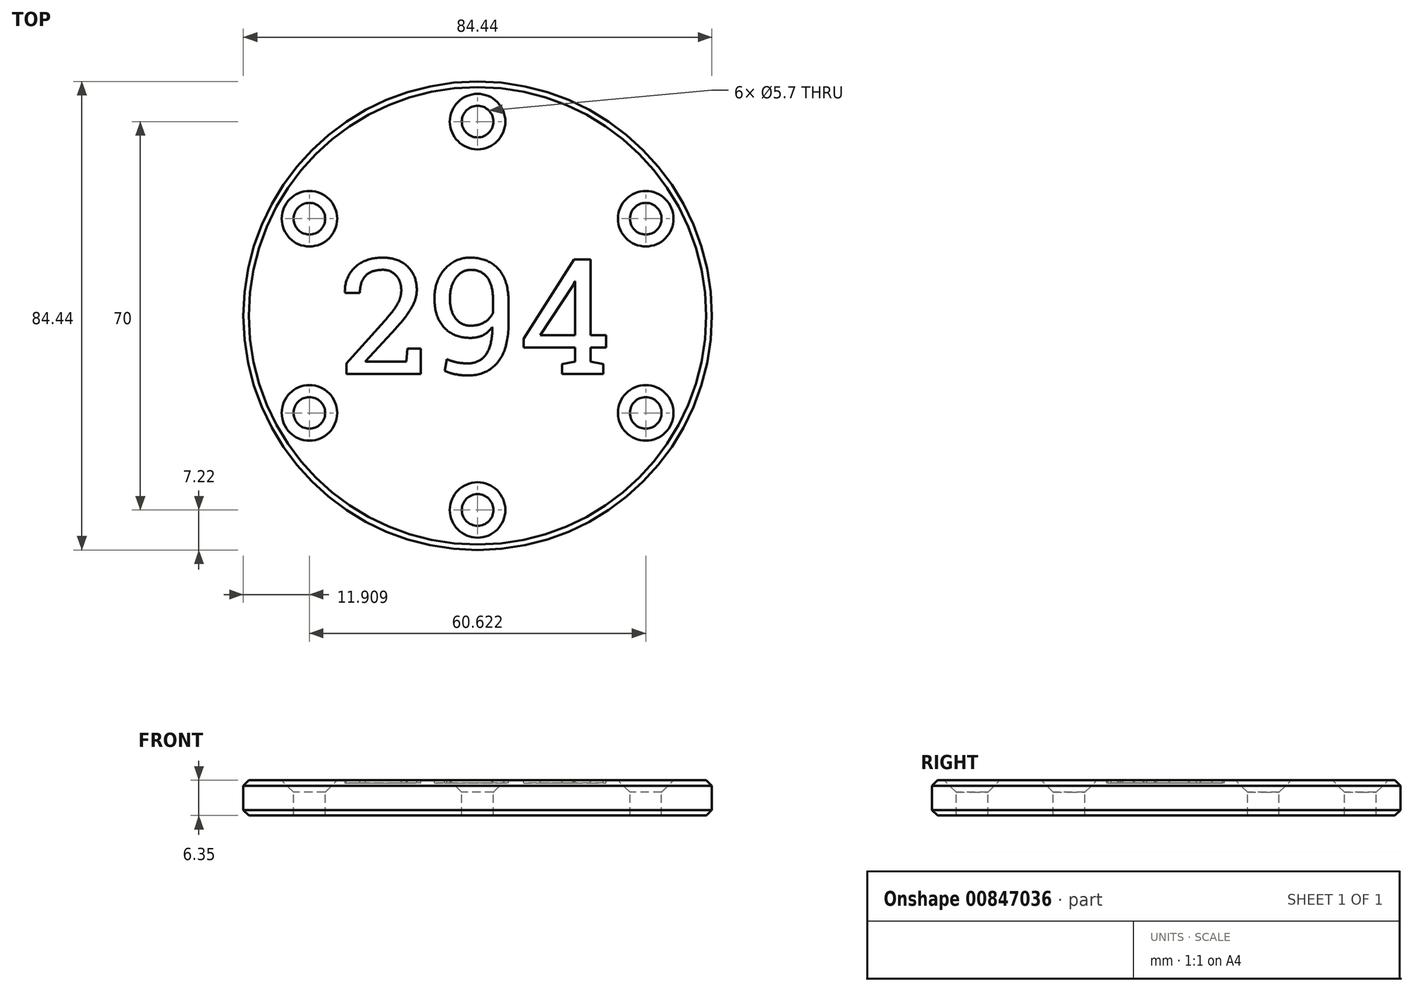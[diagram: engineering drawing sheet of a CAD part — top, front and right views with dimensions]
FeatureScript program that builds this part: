
annotation { "Feature Type Name" : "Feature", "Feature Type Description" : "" }
export const myFeature = defineFeature(function(context is Context, id is Id, definition is map)
    precondition{}
    {
        {
            var Q0;
            Q0=qCreatedBy(makeId("Top.planeOp"),FACE);
            var sketch = newSketch(context, id + "F0", { "sketchPlane" : qUnion([Q0])});
            skCircle(sketch, "E0", {"center": v(0, 0) * mm, "radius": 42.22 * mm});
            skCircle(sketch, "E1", {"center": v(0, 0) * mm, "radius": 24 * mm});
            skCircle(sketch, "E2.cCircle", {"center": v(0, 0) * mm, "radius": 35 * mm, "construction": true});
            skLineSegment(sketch, "E2.0", {"start": v(0, 35) * mm, "end": v(30.31, 17.5) * mm});
            skLineSegment(sketch, "E2.1", {"start": v(30.31, 17.5) * mm, "end": v(30.31, -17.5) * mm});
            skLineSegment(sketch, "E2.2", {"start": v(30.31, -17.5) * mm, "end": v(0, -35) * mm});
            skLineSegment(sketch, "E2.3", {"start": v(0, -35) * mm, "end": v(-30.31, -17.5) * mm});
            skLineSegment(sketch, "E2.4", {"start": v(-30.31, -17.5) * mm, "end": v(-30.31, 17.5) * mm});
            skLineSegment(sketch, "E2.5", {"start": v(-30.31, 17.5) * mm, "end": v(0, 35) * mm});
            skCircle(sketch, "E3", {"center": v(0, 35) * mm, "radius": 3 * mm});
            skCircle(sketch, "E4", {"center": v(30.31, 17.5) * mm, "radius": 3 * mm});
            skCircle(sketch, "E5", {"center": v(30.31, -17.5) * mm, "radius": 3 * mm});
            skCircle(sketch, "E6", {"center": v(0, -35) * mm, "radius": 3 * mm});
            skCircle(sketch, "E7", {"center": v(-30.31, -17.5) * mm, "radius": 3 * mm});
            skCircle(sketch, "E8", {"center": v(-30.31, 17.5) * mm, "radius": 3 * mm});
            skSolve(sketch);
        }
        {
            var Q0;
            Q0=makeQuery(id+"F0.imprint","IMPRINT",FACE,{"disambiguationData":[TD([[makeQuery(id+"F0.imprint","IMPRINT",EDGE,{"derivedFrom":sQuery(id+"F0.wireOp",EDGE,"E1")}),1.0]])]});
            var Q1;
            Q1=makeQuery(id+"F0.imprint","IMPRINT",FACE,{"disambiguationData":[TD([[makeQuery(id+"F0.imprint","IMPRINT",EDGE,{"derivedFrom":sQuery(id+"F0.wireOp",EDGE,"E0")}),1.0]])]});
            var Q2;
            {var subQ0=sQuery(id+"F0.wireOp",EDGE,"E2.4");var subQ1=sQuery(id+"F0.wireOp",EDGE,"E2.3");var subQ2=makeQuery(id+"F0.imprint","INTERSECT",VERTEX,{"derivedFrom":[subQ1,subQ0]});Q2=makeQuery(id+"F0.imprint","IMPRINT",FACE,{"disambiguationData":[TD([[makeQuery(id+"F0.imprint","IMPRINT",EDGE,{"disambiguationData":[TD([[subQ2,1.0]])],"derivedFrom":subQ1}),1.0]])]});}
            var Q3;
            Q3=makeQuery(id+"F0.imprint","IMPRINT",FACE,{"disambiguationData":[TD([[makeQuery(id+"F0.imprint","IMPRINT",EDGE,{"derivedFrom":sQuery(id+"F0.wireOp",EDGE,"E1")}),-1.0]])]});
            var Q4;
            {var subQ0=sQuery(id+"F0.wireOp",EDGE,"E2.4");var subQ1=sQuery(id+"F0.wireOp",EDGE,"E2.3");var subQ2=makeQuery(id+"F0.imprint","INTERSECT",VERTEX,{"derivedFrom":[subQ1,subQ0]});Q4=makeQuery(id+"F0.imprint","IMPRINT",FACE,{"disambiguationData":[TD([[makeQuery(id+"F0.imprint","IMPRINT",EDGE,{"disambiguationData":[TD([[subQ2,1.0]])],"derivedFrom":subQ1}),-1.0]])]});}
            var Q5;
            {var subQ0=sQuery(id+"F0.wireOp",EDGE,"E2.5");var subQ1=sQuery(id+"F0.wireOp",EDGE,"E2.4");var subQ2=makeQuery(id+"F0.imprint","INTERSECT",VERTEX,{"derivedFrom":[subQ1,subQ0]});Q5=makeQuery(id+"F0.imprint","IMPRINT",FACE,{"disambiguationData":[TD([[makeQuery(id+"F0.imprint","IMPRINT",EDGE,{"disambiguationData":[TD([[subQ2,1.0]])],"derivedFrom":subQ1}),-1.0]])]});}
            var Q6;
            {var subQ0=sQuery(id+"F0.wireOp",EDGE,"E2.5");var subQ1=sQuery(id+"F0.wireOp",EDGE,"E2.4");var subQ2=makeQuery(id+"F0.imprint","INTERSECT",VERTEX,{"derivedFrom":[subQ1,subQ0]});Q6=makeQuery(id+"F0.imprint","IMPRINT",FACE,{"disambiguationData":[TD([[makeQuery(id+"F0.imprint","IMPRINT",EDGE,{"disambiguationData":[TD([[subQ2,1.0]])],"derivedFrom":subQ1}),1.0]])]});}
            var Q7;
            {var subQ0=sQuery(id+"F0.wireOp",EDGE,"E2.5");var subQ1=sQuery(id+"F0.wireOp",EDGE,"E2.0");var subQ2=makeQuery(id+"F0.imprint","INTERSECT",VERTEX,{"derivedFrom":[subQ1,subQ0]});Q7=makeQuery(id+"F0.imprint","IMPRINT",FACE,{"disambiguationData":[TD([[makeQuery(id+"F0.imprint","IMPRINT",EDGE,{"disambiguationData":[TD([[subQ2,-1.0]])],"derivedFrom":subQ1}),-1.0]])]});}
            var Q8;
            {var subQ0=sQuery(id+"F0.wireOp",EDGE,"E2.5");var subQ1=sQuery(id+"F0.wireOp",EDGE,"E2.0");var subQ2=makeQuery(id+"F0.imprint","INTERSECT",VERTEX,{"derivedFrom":[subQ1,subQ0]});Q8=makeQuery(id+"F0.imprint","IMPRINT",FACE,{"disambiguationData":[TD([[makeQuery(id+"F0.imprint","IMPRINT",EDGE,{"disambiguationData":[TD([[subQ2,-1.0]])],"derivedFrom":subQ1}),1.0]])]});}
            var Q9;
            {var subQ0=sQuery(id+"F0.wireOp",EDGE,"E2.1");var subQ1=sQuery(id+"F0.wireOp",EDGE,"E2.0");var subQ2=makeQuery(id+"F0.imprint","INTERSECT",VERTEX,{"derivedFrom":[subQ1,subQ0]});Q9=makeQuery(id+"F0.imprint","IMPRINT",FACE,{"disambiguationData":[TD([[makeQuery(id+"F0.imprint","IMPRINT",EDGE,{"disambiguationData":[TD([[subQ2,1.0]])],"derivedFrom":subQ1}),-1.0]])]});}
            var Q10;
            {var subQ0=sQuery(id+"F0.wireOp",EDGE,"E2.1");var subQ1=sQuery(id+"F0.wireOp",EDGE,"E2.0");var subQ2=makeQuery(id+"F0.imprint","INTERSECT",VERTEX,{"derivedFrom":[subQ1,subQ0]});Q10=makeQuery(id+"F0.imprint","IMPRINT",FACE,{"disambiguationData":[TD([[makeQuery(id+"F0.imprint","IMPRINT",EDGE,{"disambiguationData":[TD([[subQ2,1.0]])],"derivedFrom":subQ1}),1.0]])]});}
            var Q11;
            {var subQ0=sQuery(id+"F0.wireOp",EDGE,"E2.2");var subQ1=sQuery(id+"F0.wireOp",EDGE,"E2.1");var subQ2=makeQuery(id+"F0.imprint","INTERSECT",VERTEX,{"derivedFrom":[subQ1,subQ0]});Q11=makeQuery(id+"F0.imprint","IMPRINT",FACE,{"disambiguationData":[TD([[makeQuery(id+"F0.imprint","IMPRINT",EDGE,{"disambiguationData":[TD([[subQ2,1.0]])],"derivedFrom":subQ1}),-1.0]])]});}
            var Q12;
            {var subQ0=sQuery(id+"F0.wireOp",EDGE,"E2.2");var subQ1=sQuery(id+"F0.wireOp",EDGE,"E2.1");var subQ2=makeQuery(id+"F0.imprint","INTERSECT",VERTEX,{"derivedFrom":[subQ1,subQ0]});Q12=makeQuery(id+"F0.imprint","IMPRINT",FACE,{"disambiguationData":[TD([[makeQuery(id+"F0.imprint","IMPRINT",EDGE,{"disambiguationData":[TD([[subQ2,1.0]])],"derivedFrom":subQ1}),1.0]])]});}
            var Q13;
            {var subQ0=sQuery(id+"F0.wireOp",EDGE,"E2.3");var subQ1=sQuery(id+"F0.wireOp",EDGE,"E2.2");var subQ2=makeQuery(id+"F0.imprint","INTERSECT",VERTEX,{"derivedFrom":[subQ1,subQ0]});Q13=makeQuery(id+"F0.imprint","IMPRINT",FACE,{"disambiguationData":[TD([[makeQuery(id+"F0.imprint","IMPRINT",EDGE,{"disambiguationData":[TD([[subQ2,1.0]])],"derivedFrom":subQ1}),-1.0]])]});}
            var Q14;
            {var subQ0=sQuery(id+"F0.wireOp",EDGE,"E2.3");var subQ1=sQuery(id+"F0.wireOp",EDGE,"E2.2");var subQ2=makeQuery(id+"F0.imprint","INTERSECT",VERTEX,{"derivedFrom":[subQ1,subQ0]});Q14=makeQuery(id+"F0.imprint","IMPRINT",FACE,{"disambiguationData":[TD([[makeQuery(id+"F0.imprint","IMPRINT",EDGE,{"disambiguationData":[TD([[subQ2,1.0]])],"derivedFrom":subQ1}),1.0]])]});}
            extrude(context, id + "F1", {"entities" : qUnion([Q0, Q1, Q2, Q3, Q4, Q5, Q6, Q7, Q8, Q9, Q10, Q11, Q12, Q13, Q14]), "depth" : 6.35 * mm, "offsetDistance" : 25 * mm});
        }
        {
            var Q0;
            Q0=qCreatedBy(makeId("Top.planeOp"),FACE);
            cPlane(context, id + "F2", {"entities" : qUnion([Q0]), "cplaneType" : CPlaneType.OFFSET, "offset" : 6.35 * mm, "width" : 150 * mm, "height" : 150 * mm});
        }
        {
            var Q0;
            Q0=qCreatedBy(id+"F2.planeOp",FACE);
            var sketch = newSketch(context, id + "F3", { "sketchPlane" : qUnion([Q0])});
            skCircle(sketch, "E9", {"center": v(0, 0) * mm, "radius": 42.22 * mm});
            skCircle(sketch, "E10", {"center": v(0, 0) * mm, "radius": 24 * mm});
            skCircle(sketch, "E11.cCircle", {"center": v(0, 0) * mm, "radius": 35 * mm, "construction": true});
            skLineSegment(sketch, "E11.0", {"start": v(0, 35) * mm, "end": v(30.31, 17.5) * mm});
            skLineSegment(sketch, "E11.1", {"start": v(30.31, 17.5) * mm, "end": v(30.31, -17.5) * mm});
            skLineSegment(sketch, "E11.2", {"start": v(30.31, -17.5) * mm, "end": v(0, -35) * mm});
            skLineSegment(sketch, "E11.3", {"start": v(0, -35) * mm, "end": v(-30.31, -17.5) * mm});
            skLineSegment(sketch, "E11.4", {"start": v(-30.31, -17.5) * mm, "end": v(-30.31, 17.5) * mm});
            skLineSegment(sketch, "E11.5", {"start": v(-30.31, 17.5) * mm, "end": v(0, 35) * mm});
            skCircle(sketch, "E12", {"center": v(0, 35) * mm, "radius": 3 * mm});
            skCircle(sketch, "E13", {"center": v(30.31, 17.5) * mm, "radius": 3 * mm});
            skCircle(sketch, "E14", {"center": v(30.31, -17.5) * mm, "radius": 3 * mm});
            skCircle(sketch, "E15", {"center": v(0, -35) * mm, "radius": 3 * mm});
            skCircle(sketch, "E16", {"center": v(-30.31, -17.5) * mm, "radius": 3 * mm});
            skCircle(sketch, "E17", {"center": v(-30.31, 17.5) * mm, "radius": 3 * mm});
            skSolve(sketch);
        }
        {
            var Q0;
            Q0=sQuery(id+"F3.wireOp",VERTEX,"E11.4.end");
            var Q1;
            Q1=sQuery(id+"F3.wireOp",VERTEX,"E11.0.start");
            var Q2;
            Q2=sQuery(id+"F3.wireOp",VERTEX,"E11.0.end");
            var Q3;
            Q3=sQuery(id+"F3.wireOp",VERTEX,"E11.1.end");
            var Q4;
            Q4=sQuery(id+"F3.wireOp",VERTEX,"E11.2.end");
            var Q5;
            Q5=sQuery(id+"F3.wireOp",VERTEX,"E11.3.end");
            var Q6;
            Q6=makeQuery(id+"F1.opExtrude","SWEPT_BODY",BODY,{"disambiguationData":[OSD([sQuery(id+"F0.wireOp",EDGE,"E0")])]});
            hole(context, id + "F4", {"style" : HoleStyle.C_SINK, "endStyle" : HoleEndStyle.THROUGH, "holeDiameter" : 5.7 * mm, "cSinkDiameter" : 10 * mm, "cSinkAngle" : 90 * degree, "majorDiameter" : 5 * mm, "isTappedThrough" : true, "tappedDepth" : 12 * mm, "tapClearance" : 3, "locations" : qUnion([Q0, Q1, Q2, Q3, Q4, Q5]), "scope" : qUnion([Q6])});
        }
        {
            var Q0;
            Q0=makeQuery(id+"F1.opExtrude","CAP_EDGE",EDGE,{"disambiguationData":[OSD([sQuery(id+"F0.wireOp",EDGE,"E0")])],"isStart":false});
            chamfer(context, id + "F5", {"entities" : qUnion([Q0]), "width" : 1 * mm, "tangentPropagation" : true});
        }
        {
            var Q0;
            Q0=makeQuery(id+"F1.opExtrude","CAP_EDGE",EDGE,{"disambiguationData":[OSD([sQuery(id+"F0.wireOp",EDGE,"E0")])],"isStart":true});
            chamfer(context, id + "F6", {"entities" : qUnion([Q0]), "width" : 1 * mm, "tangentPropagation" : true});
        }
        {
            var Q0;
            Q0=qCreatedBy(id+"F2.planeOp",FACE);
            var sketch = newSketch(context, id + "F7", { "sketchPlane" : qUnion([Q0])});
            skText(sketch, "E18", { "text": "294", "fontName": "RobotoSlab-Regular.ttf"});
            const initialGuessF7  = {"E18": [-0.025, -0.01046, 1, 0, 0.02091]};
            skSetInitialGuess(sketch, initialGuessF7);
            skSolve(sketch);
        }
        {
            var Q0;
            Q0 = qSketchRegion(id + "F7", true);
            extrude(context, id + "F8", {"entities" : qUnion([Q0]), "operationType" : NewBodyOperationType.REMOVE, "oppositeDirection" : true, "depth" : .5 * mm, "offsetDistance" : 25 * mm});
        }
    });
